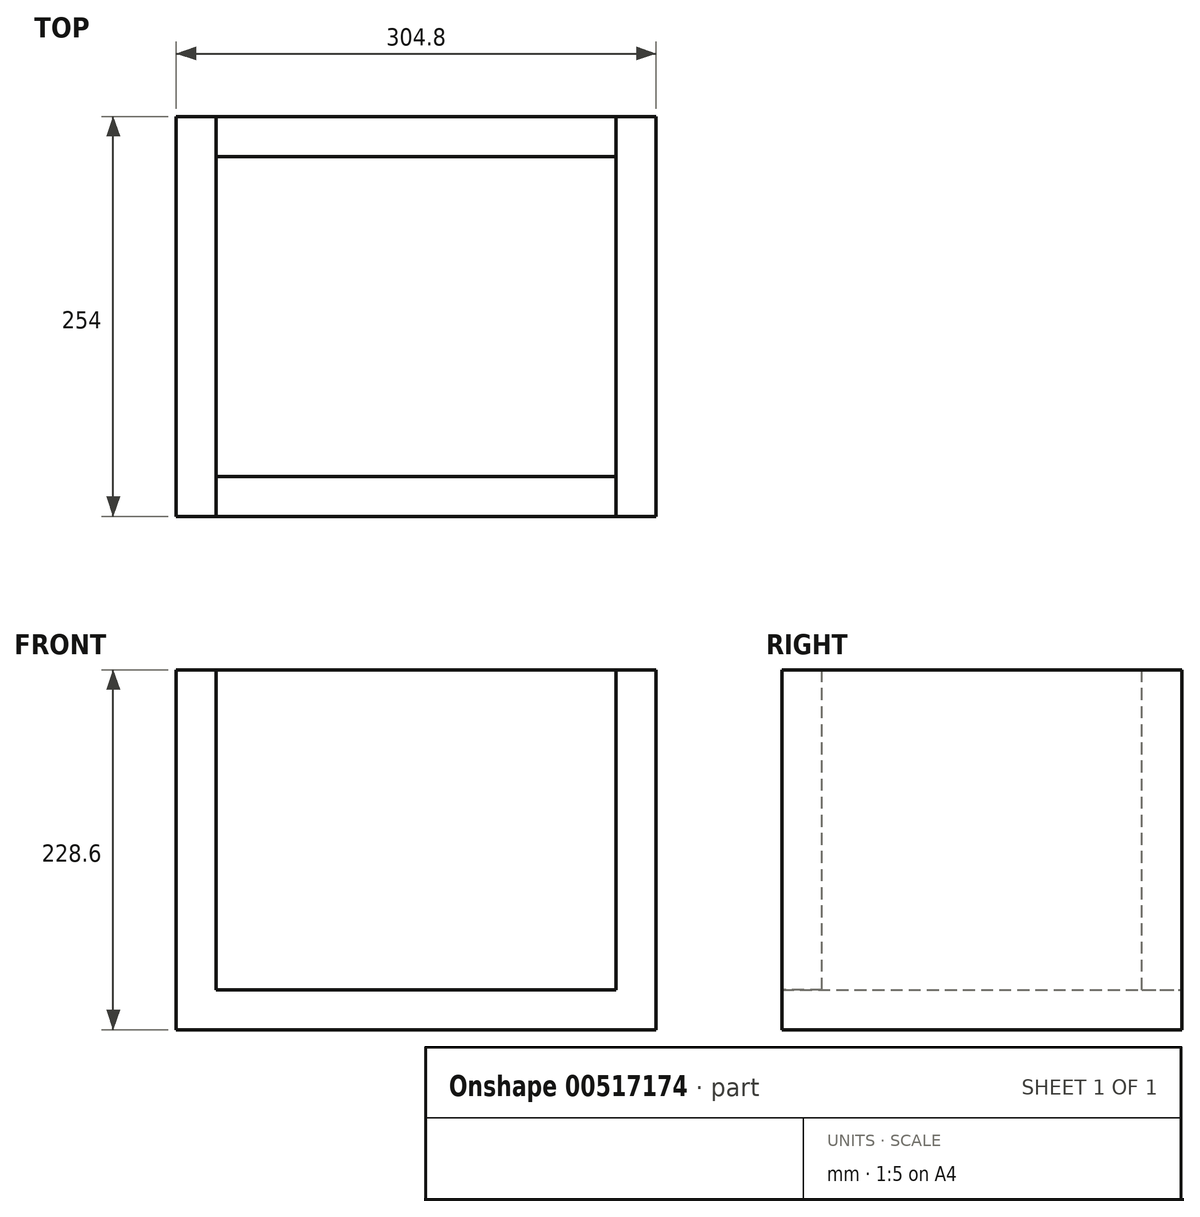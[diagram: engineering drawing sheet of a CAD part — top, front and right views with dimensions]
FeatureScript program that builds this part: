
annotation { "Feature Type Name" : "Feature", "Feature Type Description" : "" }
export const myFeature = defineFeature(function(context is Context, id is Id, definition is map)
    precondition{}
    {
        {
            var Q0;
            Q0=qCreatedBy(makeId("Front.planeOp"),FACE);
            var sketch = newSketch(context, id + "F0", { "sketchPlane" : qUnion([Q0])});
            skLineSegment(sketch, "E0", {"start": v(0, 0) * mm, "end": v(-127, 0) * mm});
            skLineSegment(sketch, "E1", {"start": v(0, 0) * mm, "end": v(127, 0) * mm});
            skLineSegment(sketch, "E2", {"start": v(127, 0) * mm, "end": v(127, 203.2) * mm});
            skLineSegment(sketch, "E3", {"start": v(-127, 0) * mm, "end": v(-127, 203.2) * mm});
            skLineSegment(sketch, "E4", {"start": v(-127, 203.2) * mm, "end": v(-152.4, 203.2) * mm});
            skLineSegment(sketch, "E5", {"start": v(-152.4, 203.2) * mm, "end": v(-152.4, -25.4) * mm});
            skLineSegment(sketch, "E6", {"start": v(-152.4, -25.4) * mm, "end": v(152.4, -25.4) * mm});
            skLineSegment(sketch, "E7", {"start": v(152.4, -25.4) * mm, "end": v(152.4, 203.2) * mm});
            skLineSegment(sketch, "E8", {"start": v(152.4, 203.2) * mm, "end": v(127, 203.2) * mm});
            skSolve(sketch);
        }
        {
            var Q0;
            Q0 = qSketchRegion(id + "F0", true);
            extrude(context, id + "F1", {"entities" : qUnion([Q0]), "depth" : 254 * mm, "offsetDistance" : 25.4 * mm});
        }
        {
            var Q0;
            Q0=makeQuery(id+"F1.opExtrude","CAP_FACE",FACE,{"disambiguationData":[OSD([sQuery(id+"F0.wireOp",EDGE,"E0"),sQuery(id+"F0.wireOp",EDGE,"E1"),sQuery(id+"F0.wireOp",EDGE,"E2"),sQuery(id+"F0.wireOp",EDGE,"E3"),sQuery(id+"F0.wireOp",EDGE,"E4"),sQuery(id+"F0.wireOp",EDGE,"E5"),sQuery(id+"F0.wireOp",EDGE,"E6"),sQuery(id+"F0.wireOp",EDGE,"E7"),sQuery(id+"F0.wireOp",EDGE,"E8")])],"isStart":false});
            var sketch = newSketch(context, id + "F2", { "sketchPlane" : qUnion([Q0])});
            skLineSegment(sketch, "E9", {"start": v(-127, 203.2) * mm, "end": v(127, 203.2) * mm});
            skSolve(sketch);
        }
        {
            var Q0;
            Q0 = qSketchRegion(id + "F2", true);
            var Q1;
            Q1=makeQuery(id+"F2.imprint","IMPRINT",FACE,{"disambiguationData":[TD([[makeQuery(id+"F2.imprint","IMPRINT",EDGE,{"derivedFrom":sQuery(id+"F2.wireOp",EDGE,"E9")}),-1.0]])]});
            extrude(context, id + "F3", {"entities" : qUnion([Q0, Q1]), "oppositeDirection" : true, "depth" : 25.4 * mm, "offsetDistance" : 25.4 * mm});
        }
        {
            var Q0;
            Q0=makeQuery(id+"F1.opExtrude","CAP_FACE",FACE,{"disambiguationData":[OSD([sQuery(id+"F0.wireOp",EDGE,"E0"),sQuery(id+"F0.wireOp",EDGE,"E1"),sQuery(id+"F0.wireOp",EDGE,"E2"),sQuery(id+"F0.wireOp",EDGE,"E3"),sQuery(id+"F0.wireOp",EDGE,"E4"),sQuery(id+"F0.wireOp",EDGE,"E5"),sQuery(id+"F0.wireOp",EDGE,"E6"),sQuery(id+"F0.wireOp",EDGE,"E7"),sQuery(id+"F0.wireOp",EDGE,"E8")])],"isStart":true});
            var sketch = newSketch(context, id + "F4", { "sketchPlane" : qUnion([Q0])});
            skLineSegment(sketch, "E10", {"start": v(-127, 203.2) * mm, "end": v(127, 203.2) * mm});
            skLineSegment(sketch, "E11", {"start": v(-127, 203.2) * mm, "end": v(-127, 0) * mm});
            skLineSegment(sketch, "E12", {"start": v(-127, 0) * mm, "end": v(127, 0) * mm});
            skLineSegment(sketch, "E13", {"start": v(127, 0) * mm, "end": v(127, 203.2) * mm});
            skSolve(sketch);
        }
        {
            var Q0;
            Q0 = qSketchRegion(id + "F4", true);
            extrude(context, id + "F5", {"entities" : qUnion([Q0]), "oppositeDirection" : true, "depth" : 25.4 * mm, "offsetDistance" : 25.4 * mm});
        }
    });
